FCSTD DOCUMENT  (FreeCAD 0.20R29603 (Git))
Label: letterplate_13_13_V2_freecad
License: All rights reserved
LicenseURL: http://en.wikipedia.org/wiki/All_rights_reserved
objects: Part::Part2DObjectPython×171, App::Part×1
note: 171 computed .brp shape members not serialized (recipe doc carries the construction recipe); baked Part::Feature solids carry a one-line shape summary decoded from their .brp

FEATURE [Part::Part2DObjectPython] Circle  # Draft 2D object (typed FeaturePython)
  Area = 0
  FirstAngle = 0
  LastAngle = 0
  MakeFace = true
  Placement = pos=(275,502.778,0) rot=(0,0,1;0rad)
  Radius = 2.56
FEATURE [Part::Part2DObjectPython] ShapeString  # Draft 2D object (typed FeaturePython)
  FontFile = <path> macros/fonts/LiberationMono-V2.ttf
  MakeFace = true
  Placement = pos=(64.8,463.626,0) rot=(0,0,1;0rad)
  Size = 25.5
  Tracking = 0
FEATURE [Part::Part2DObjectPython] ShapeString001  # Draft 2D object (typed FeaturePython)
  FontFile = <path> macros/fonts/LiberationMono-V2.ttf
  MakeFace = true
  Placement = pos=(98.1333,463.626,0) rot=(0,0,1;0rad)
  Size = 25.5
  Tracking = 0
FEATURE [Part::Part2DObjectPython] ShapeString002  # Draft 2D object (typed FeaturePython)
  FontFile = <path> macros/fonts/LiberationMono-V2.ttf
  MakeFace = true
  Placement = pos=(131.467,463.626,0) rot=(0,0,1;0rad)
  Size = 25.5
  Tracking = 0
FEATURE [Part::Part2DObjectPython] ShapeString003  # Draft 2D object (typed FeaturePython)
  FontFile = <path> macros/fonts/LiberationMono-V2.ttf
  MakeFace = true
  Placement = pos=(164.8,463.626,0) rot=(0,0,1;0rad)
  Size = 25.5
  Tracking = 0
FEATURE [Part::Part2DObjectPython] ShapeString004  # Draft 2D object (typed FeaturePython)
  FontFile = <path> macros/fonts/LiberationMono-V2.ttf
  MakeFace = true
  Placement = pos=(198.133,463.626,0) rot=(0,0,1;0rad)
  Size = 25.5
  Tracking = 0
FEATURE [Part::Part2DObjectPython] ShapeString005  # Draft 2D object (typed FeaturePython)
  FontFile = <path> macros/fonts/LiberationMono-V2.ttf
  MakeFace = true
  Placement = pos=(231.467,463.626,0) rot=(0,0,1;0rad)
  Size = 25.5
  Tracking = 0
FEATURE [Part::Part2DObjectPython] ShapeString006  # Draft 2D object (typed FeaturePython)
  FontFile = <path> macros/fonts/LiberationMono-V2.ttf
  MakeFace = true
  Placement = pos=(264.8,463.626,0) rot=(0,0,1;0rad)
  Size = 25.5
  Tracking = 0
FEATURE [Part::Part2DObjectPython] ShapeString007  # Draft 2D object (typed FeaturePython)
  FontFile = <path> macros/fonts/LiberationMono-V2.ttf
  MakeFace = true
  Placement = pos=(298.133,463.626,0) rot=(0,0,1;0rad)
  Size = 25.5
  Tracking = 0
FEATURE [Part::Part2DObjectPython] ShapeString008  # Draft 2D object (typed FeaturePython)
  FontFile = <path> macros/fonts/LiberationMono-V2.ttf
  MakeFace = true
  Placement = pos=(331.467,463.626,0) rot=(0,0,1;0rad)
  Size = 25.5
  Tracking = 0
FEATURE [Part::Part2DObjectPython] ShapeString009  # Draft 2D object (typed FeaturePython)
  FontFile = <path> macros/fonts/LiberationMono-V2.ttf
  MakeFace = true
  Placement = pos=(364.8,463.626,0) rot=(0,0,1;0rad)
  Size = 25.5
  Tracking = 0
FEATURE [Part::Part2DObjectPython] ShapeString010  # Draft 2D object (typed FeaturePython)
  FontFile = <path> macros/fonts/LiberationMono-V2.ttf
  MakeFace = true
  Placement = pos=(398.133,463.626,0) rot=(0,0,1;0rad)
  Size = 25.5
  Tracking = 0
FEATURE [Part::Part2DObjectPython] ShapeString011  # Draft 2D object (typed FeaturePython)
  FontFile = <path> macros/fonts/LiberationMono-V2.ttf
  MakeFace = true
  Placement = pos=(431.467,463.626,0) rot=(0,0,1;0rad)
  Size = 25.5
  Tracking = 0
FEATURE [Part::Part2DObjectPython] ShapeString012  # Draft 2D object (typed FeaturePython)
  FontFile = <path> macros/fonts/LiberationMono-V2.ttf
  MakeFace = true
  Placement = pos=(464.8,463.626,0) rot=(0,0,1;0rad)
  Size = 25.5
  Tracking = 0
FEATURE [Part::Part2DObjectPython] ShapeString013  # Draft 2D object (typed FeaturePython)
  FontFile = <path> macros/fonts/LiberationMono-V2.ttf
  MakeFace = true
  Placement = pos=(64.8,430.293,0) rot=(0,0,1;0rad)
  Size = 25.5
  Tracking = 0
FEATURE [Part::Part2DObjectPython] ShapeString014  # Draft 2D object (typed FeaturePython)
  FontFile = <path> macros/fonts/LiberationMono-V2.ttf
  MakeFace = true
  Placement = pos=(98.1333,430.293,0) rot=(0,0,1;0rad)
  Size = 25.5
  String = S
  Tracking = 0
FEATURE [Part::Part2DObjectPython] ShapeString015  # Draft 2D object (typed FeaturePython)
  FontFile = <path> macros/fonts/LiberationMono-V2.ttf
  MakeFace = true
  Placement = pos=(131.467,430.293,0) rot=(0,0,1;0rad)
  Size = 25.5
  String = O
  Tracking = 0
FEATURE [Part::Part2DObjectPython] ShapeString016  # Draft 2D object (typed FeaturePython)
  FontFile = <path> macros/fonts/LiberationMono-V2.ttf
  MakeFace = true
  Placement = pos=(164.8,430.293,0) rot=(0,0,1;0rad)
  Size = 25.5
  String = N
  Tracking = 0
FEATURE [Part::Part2DObjectPython] ShapeString017  # Draft 2D object (typed FeaturePython)
  FontFile = <path> macros/fonts/LiberationMono-V2.ttf
  MakeFace = true
  Placement = pos=(198.133,430.293,0) rot=(0,0,1;0rad)
  Size = 25.5
  String = O
  Tracking = 0
FEATURE [Part::Part2DObjectPython] ShapeString018  # Draft 2D object (typed FeaturePython)
  FontFile = <path> macros/fonts/LiberationMono-V2.ttf
  MakeFace = true
  Placement = pos=(231.467,430.293,0) rot=(0,0,1;0rad)
  Size = 25.5
  String = È
  Tracking = 0
FEATURE [Part::Part2DObjectPython] ShapeString019  # Draft 2D object (typed FeaturePython)
  FontFile = <path> macros/fonts/LiberationMono-V2.ttf
  MakeFace = true
  Placement = pos=(264.8,430.293,0) rot=(0,0,1;0rad)
  Size = 25.5
  String = L
  Tracking = 0
FEATURE [Part::Part2DObjectPython] ShapeString020  # Draft 2D object (typed FeaturePython)
  FontFile = <path> macros/fonts/LiberationMono-V2.ttf
  MakeFace = true
  Placement = pos=(298.133,430.293,0) rot=(0,0,1;0rad)
  Size = 25.5
  String = E
  Tracking = 0
FEATURE [Part::Part2DObjectPython] ShapeString021  # Draft 2D object (typed FeaturePython)
  FontFile = <path> macros/fonts/LiberationMono-V2.ttf
  MakeFace = true
  Placement = pos=(331.467,430.293,0) rot=(0,0,1;0rad)
  Size = 25.5
  String = R
  Tracking = 0
FEATURE [Part::Part2DObjectPython] ShapeString022  # Draft 2D object (typed FeaturePython)
  FontFile = <path> macros/fonts/LiberationMono-V2.ttf
  MakeFace = true
  Placement = pos=(364.8,430.293,0) rot=(0,0,1;0rad)
  Size = 25.5
  String = D
  Tracking = 0
FEATURE [Part::Part2DObjectPython] ShapeString023  # Draft 2D object (typed FeaturePython)
  FontFile = <path> macros/fonts/LiberationMono-V2.ttf
  MakeFace = true
  Placement = pos=(398.133,430.293,0) rot=(0,0,1;0rad)
  Size = 25.5
  String = U
  Tracking = 0
FEATURE [Part::Part2DObjectPython] ShapeString024  # Draft 2D object (typed FeaturePython)
  FontFile = <path> macros/fonts/LiberationMono-V2.ttf
  MakeFace = true
  Placement = pos=(431.467,430.293,0) rot=(0,0,1;0rad)
  Size = 25.5
  String = E
  Tracking = 0
FEATURE [Part::Part2DObjectPython] ShapeString025  # Draft 2D object (typed FeaturePython)
  FontFile = <path> macros/fonts/LiberationMono-V2.ttf
  MakeFace = true
  Placement = pos=(464.8,430.293,0) rot=(0,0,1;0rad)
  Size = 25.5
  Tracking = 0
FEATURE [Part::Part2DObjectPython] ShapeString026  # Draft 2D object (typed FeaturePython)
  FontFile = <path> macros/fonts/LiberationMono-V2.ttf
  MakeFace = true
  Placement = pos=(64.8,396.959,0) rot=(0,0,1;0rad)
  Size = 25.5
  Tracking = 0
FEATURE [Part::Part2DObjectPython] ShapeString027  # Draft 2D object (typed FeaturePython)
  FontFile = <path> macros/fonts/LiberationMono-V2.ttf
  MakeFace = true
  Placement = pos=(98.1333,396.959,0) rot=(0,0,1;0rad)
  Size = 25.5
  String = L
  Tracking = 0
FEATURE [Part::Part2DObjectPython] ShapeString028  # Draft 2D object (typed FeaturePython)
  FontFile = <path> macros/fonts/LiberationMono-V2.ttf
  MakeFace = true
  Placement = pos=(131.467,396.959,0) rot=(0,0,1;0rad)
  Size = 25.5
  String = U
  Tracking = 0
FEATURE [Part::Part2DObjectPython] ShapeString029  # Draft 2D object (typed FeaturePython)
  FontFile = <path> macros/fonts/LiberationMono-V2.ttf
  MakeFace = true
  Placement = pos=(164.8,396.959,0) rot=(0,0,1;0rad)
  Size = 25.5
  String = N
  Tracking = 0
FEATURE [Part::Part2DObjectPython] ShapeString030  # Draft 2D object (typed FeaturePython)
  FontFile = <path> macros/fonts/LiberationMono-V2.ttf
  MakeFace = true
  Placement = pos=(198.133,396.959,0) rot=(0,0,1;0rad)
  Size = 25.5
  String = A
  Tracking = 0
FEATURE [Part::Part2DObjectPython] ShapeString031  # Draft 2D object (typed FeaturePython)
  FontFile = <path> macros/fonts/LiberationMono-V2.ttf
  MakeFace = true
  Placement = pos=(231.467,396.959,0) rot=(0,0,1;0rad)
  Size = 25.5
  String = Q
  Tracking = 0
FEATURE [Part::Part2DObjectPython] ShapeString032  # Draft 2D object (typed FeaturePython)
  FontFile = <path> macros/fonts/LiberationMono-V2.ttf
  MakeFace = true
  Placement = pos=(264.8,396.959,0) rot=(0,0,1;0rad)
  Size = 25.5
  String = U
  Tracking = 0
FEATURE [Part::Part2DObjectPython] ShapeString033  # Draft 2D object (typed FeaturePython)
  FontFile = <path> macros/fonts/LiberationMono-V2.ttf
  MakeFace = true
  Placement = pos=(298.133,396.959,0) rot=(0,0,1;0rad)
  Size = 25.5
  String = A
  Tracking = 0
FEATURE [Part::Part2DObjectPython] ShapeString034  # Draft 2D object (typed FeaturePython)
  FontFile = <path> macros/fonts/LiberationMono-V2.ttf
  MakeFace = true
  Placement = pos=(331.467,396.959,0) rot=(0,0,1;0rad)
  Size = 25.5
  String = T
  Tracking = 0
FEATURE [Part::Part2DObjectPython] ShapeString035  # Draft 2D object (typed FeaturePython)
  FontFile = <path> macros/fonts/LiberationMono-V2.ttf
  MakeFace = true
  Placement = pos=(364.8,396.959,0) rot=(0,0,1;0rad)
  Size = 25.5
  String = T
  Tracking = 0
FEATURE [Part::Part2DObjectPython] ShapeString036  # Draft 2D object (typed FeaturePython)
  FontFile = <path> macros/fonts/LiberationMono-V2.ttf
  MakeFace = true
  Placement = pos=(398.133,396.959,0) rot=(0,0,1;0rad)
  Size = 25.5
  String = R
  Tracking = 0
FEATURE [Part::Part2DObjectPython] ShapeString037  # Draft 2D object (typed FeaturePython)
  FontFile = <path> macros/fonts/LiberationMono-V2.ttf
  MakeFace = true
  Placement = pos=(431.467,396.959,0) rot=(0,0,1;0rad)
  Size = 25.5
  String = O
  Tracking = 0
FEATURE [Part::Part2DObjectPython] ShapeString038  # Draft 2D object (typed FeaturePython)
  FontFile = <path> macros/fonts/LiberationMono-V2.ttf
  MakeFace = true
  Placement = pos=(464.8,396.959,0) rot=(0,0,1;0rad)
  Size = 25.5
  Tracking = 0
FEATURE [Part::Part2DObjectPython] ShapeString039  # Draft 2D object (typed FeaturePython)
  FontFile = <path> macros/fonts/LiberationMono-V2.ttf
  MakeFace = true
  Placement = pos=(64.8,363.626,0) rot=(0,0,1;0rad)
  Size = 25.5
  Tracking = 0
FEATURE [Part::Part2DObjectPython] ShapeString040  # Draft 2D object (typed FeaturePython)
  FontFile = <path> macros/fonts/LiberationMono-V2.ttf
  MakeFace = true
  Placement = pos=(98.1333,363.626,0) rot=(0,0,1;0rad)
  Size = 25.5
  String = S
  Tracking = 0
FEATURE [Part::Part2DObjectPython] ShapeString041  # Draft 2D object (typed FeaturePython)
  FontFile = <path> macros/fonts/LiberationMono-V2.ttf
  MakeFace = true
  Placement = pos=(131.467,363.626,0) rot=(0,0,1;0rad)
  Size = 25.5
  String = E
  Tracking = 0
FEATURE [Part::Part2DObjectPython] ShapeString042  # Draft 2D object (typed FeaturePython)
  FontFile = <path> macros/fonts/LiberationMono-V2.ttf
  MakeFace = true
  Placement = pos=(164.8,363.626,0) rot=(0,0,1;0rad)
  Size = 25.5
  String = T
  Tracking = 0
FEATURE [Part::Part2DObjectPython] ShapeString043  # Draft 2D object (typed FeaturePython)
  FontFile = <path> macros/fonts/LiberationMono-V2.ttf
  MakeFace = true
  Placement = pos=(198.133,363.626,0) rot=(0,0,1;0rad)
  Size = 25.5
  String = T
  Tracking = 0
FEATURE [Part::Part2DObjectPython] ShapeString044  # Draft 2D object (typed FeaturePython)
  FontFile = <path> macros/fonts/LiberationMono-V2.ttf
  MakeFace = true
  Placement = pos=(231.467,363.626,0) rot=(0,0,1;0rad)
  Size = 25.5
  String = E
  Tracking = 0
FEATURE [Part::Part2DObjectPython] ShapeString045  # Draft 2D object (typed FeaturePython)
  FontFile = <path> macros/fonts/LiberationMono-V2.ttf
  MakeFace = true
  Placement = pos=(264.8,363.626,0) rot=(0,0,1;0rad)
  Size = 25.5
  String = D
  Tracking = 0
FEATURE [Part::Part2DObjectPython] ShapeString046  # Draft 2D object (typed FeaturePython)
  FontFile = <path> macros/fonts/LiberationMono-V2.ttf
  MakeFace = true
  Placement = pos=(298.133,363.626,0) rot=(0,0,1;0rad)
  Size = 25.5
  String = O
  Tracking = 0
FEATURE [Part::Part2DObjectPython] ShapeString047  # Draft 2D object (typed FeaturePython)
  FontFile = <path> macros/fonts/LiberationMono-V2.ttf
  MakeFace = true
  Placement = pos=(331.467,363.626,0) rot=(0,0,1;0rad)
  Size = 25.5
  String = D
  Tracking = 0
FEATURE [Part::Part2DObjectPython] ShapeString048  # Draft 2D object (typed FeaturePython)
  FontFile = <path> macros/fonts/LiberationMono-V2.ttf
  MakeFace = true
  Placement = pos=(364.8,363.626,0) rot=(0,0,1;0rad)
  Size = 25.5
  String = I
  Tracking = 0
FEATURE [Part::Part2DObjectPython] ShapeString049  # Draft 2D object (typed FeaturePython)
  FontFile = <path> macros/fonts/LiberationMono-V2.ttf
  MakeFace = true
  Placement = pos=(398.133,363.626,0) rot=(0,0,1;0rad)
  Size = 25.5
  String = C
  Tracking = 0
FEATURE [Part::Part2DObjectPython] ShapeString050  # Draft 2D object (typed FeaturePython)
  FontFile = <path> macros/fonts/LiberationMono-V2.ttf
  MakeFace = true
  Placement = pos=(431.467,363.626,0) rot=(0,0,1;0rad)
  Size = 25.5
  String = I
  Tracking = 0
FEATURE [Part::Part2DObjectPython] ShapeString051  # Draft 2D object (typed FeaturePython)
  FontFile = <path> macros/fonts/LiberationMono-V2.ttf
  MakeFace = true
  Placement = pos=(464.8,363.626,0) rot=(0,0,1;0rad)
  Size = 25.5
  Tracking = 0
FEATURE [Part::Part2DObjectPython] ShapeString052  # Draft 2D object (typed FeaturePython)
  FontFile = <path> macros/fonts/LiberationMono-V2.ttf
  MakeFace = true
  Placement = pos=(64.8,330.293,0) rot=(0,0,1;0rad)
  Size = 25.5
  Tracking = 0
FEATURE [Part::Part2DObjectPython] ShapeString053  # Draft 2D object (typed FeaturePython)
  FontFile = <path> macros/fonts/LiberationMono-V2.ttf
  MakeFace = true
  Placement = pos=(98.1333,330.293,0) rot=(0,0,1;0rad)
  Size = 25.5
  String = S
  Tracking = 0
FEATURE [Part::Part2DObjectPython] ShapeString054  # Draft 2D object (typed FeaturePython)
  FontFile = <path> macros/fonts/LiberationMono-V2.ttf
  MakeFace = true
  Placement = pos=(131.467,330.293,0) rot=(0,0,1;0rad)
  Size = 25.5
  String = E
  Tracking = 0
FEATURE [Part::Part2DObjectPython] ShapeString055  # Draft 2D object (typed FeaturePython)
  FontFile = <path> macros/fonts/LiberationMono-V2.ttf
  MakeFace = true
  Placement = pos=(164.8,330.293,0) rot=(0,0,1;0rad)
  Size = 25.5
  String = I
  Tracking = 0
FEATURE [Part::Part2DObjectPython] ShapeString056  # Draft 2D object (typed FeaturePython)
  FontFile = <path> macros/fonts/LiberationMono-V2.ttf
  MakeFace = true
  Placement = pos=(198.133,330.293,0) rot=(0,0,1;0rad)
  Size = 25.5
  String = N
  Tracking = 0
FEATURE [Part::Part2DObjectPython] ShapeString057  # Draft 2D object (typed FeaturePython)
  FontFile = <path> macros/fonts/LiberationMono-V2.ttf
  MakeFace = true
  Placement = pos=(231.467,330.293,0) rot=(0,0,1;0rad)
  Size = 25.5
  String = O
  Tracking = 0
FEATURE [Part::Part2DObjectPython] ShapeString058  # Draft 2D object (typed FeaturePython)
  FontFile = <path> macros/fonts/LiberationMono-V2.ttf
  MakeFace = true
  Placement = pos=(264.8,330.293,0) rot=(0,0,1;0rad)
  Size = 25.5
  String = V
  Tracking = 0
FEATURE [Part::Part2DObjectPython] ShapeString059  # Draft 2D object (typed FeaturePython)
  FontFile = <path> macros/fonts/LiberationMono-V2.ttf
  MakeFace = true
  Placement = pos=(298.133,330.293,0) rot=(0,0,1;0rad)
  Size = 25.5
  String = E
  Tracking = 0
FEATURE [Part::Part2DObjectPython] ShapeString060  # Draft 2D object (typed FeaturePython)
  FontFile = <path> macros/fonts/LiberationMono-V2.ttf
  MakeFace = true
  Placement = pos=(331.467,330.293,0) rot=(0,0,1;0rad)
  Size = 25.5
  String = O
  Tracking = 0
FEATURE [Part::Part2DObjectPython] ShapeString061  # Draft 2D object (typed FeaturePython)
  FontFile = <path> macros/fonts/LiberationMono-V2.ttf
  MakeFace = true
  Placement = pos=(364.8,330.293,0) rot=(0,0,1;0rad)
  Size = 25.5
  String = T
  Tracking = 0
FEATURE [Part::Part2DObjectPython] ShapeString062  # Draft 2D object (typed FeaturePython)
  FontFile = <path> macros/fonts/LiberationMono-V2.ttf
  MakeFace = true
  Placement = pos=(398.133,330.293,0) rot=(0,0,1;0rad)
  Size = 25.5
  String = T
  Tracking = 0
FEATURE [Part::Part2DObjectPython] ShapeString063  # Draft 2D object (typed FeaturePython)
  FontFile = <path> macros/fonts/LiberationMono-V2.ttf
  MakeFace = true
  Placement = pos=(431.467,330.293,0) rot=(0,0,1;0rad)
  Size = 25.5
  String = O
  Tracking = 0
FEATURE [Part::Part2DObjectPython] ShapeString064  # Draft 2D object (typed FeaturePython)
  FontFile = <path> macros/fonts/LiberationMono-V2.ttf
  MakeFace = true
  Placement = pos=(464.8,330.293,0) rot=(0,0,1;0rad)
  Size = 25.5
  Tracking = 0
FEATURE [Part::Part2DObjectPython] ShapeString065  # Draft 2D object (typed FeaturePython)
  FontFile = <path> macros/fonts/LiberationMono-V2.ttf
  MakeFace = true
  Placement = pos=(64.8,296.959,0) rot=(0,0,1;0rad)
  Size = 25.5
  Tracking = 0
FEATURE [Part::Part2DObjectPython] ShapeString066  # Draft 2D object (typed FeaturePython)
  FontFile = <path> macros/fonts/LiberationMono-V2.ttf
  MakeFace = true
  Placement = pos=(98.1333,296.959,0) rot=(0,0,1;0rad)
  Size = 25.5
  String = C
  Tracking = 0
FEATURE [Part::Part2DObjectPython] ShapeString067  # Draft 2D object (typed FeaturePython)
  FontFile = <path> macros/fonts/LiberationMono-V2.ttf
  MakeFace = true
  Placement = pos=(131.467,296.959,0) rot=(0,0,1;0rad)
  Size = 25.5
  String = I
  Tracking = 0
FEATURE [Part::Part2DObjectPython] ShapeString068  # Draft 2D object (typed FeaturePython)
  FontFile = <path> macros/fonts/LiberationMono-V2.ttf
  MakeFace = true
  Placement = pos=(164.8,296.959,0) rot=(0,0,1;0rad)
  Size = 25.5
  String = N
  Tracking = 0
FEATURE [Part::Part2DObjectPython] ShapeString069  # Draft 2D object (typed FeaturePython)
  FontFile = <path> macros/fonts/LiberationMono-V2.ttf
  MakeFace = true
  Placement = pos=(198.133,296.959,0) rot=(0,0,1;0rad)
  Size = 25.5
  String = Q
  Tracking = 0
FEATURE [Part::Part2DObjectPython] ShapeString070  # Draft 2D object (typed FeaturePython)
  FontFile = <path> macros/fonts/LiberationMono-V2.ttf
  MakeFace = true
  Placement = pos=(231.467,296.959,0) rot=(0,0,1;0rad)
  Size = 25.5
  String = U
  Tracking = 0
FEATURE [Part::Part2DObjectPython] ShapeString071  # Draft 2D object (typed FeaturePython)
  FontFile = <path> macros/fonts/LiberationMono-V2.ttf
  MakeFace = true
  Placement = pos=(264.8,296.959,0) rot=(0,0,1;0rad)
  Size = 25.5
  String = E
  Tracking = 0
FEATURE [Part::Part2DObjectPython] ShapeString072  # Draft 2D object (typed FeaturePython)
  FontFile = <path> macros/fonts/LiberationMono-V2.ttf
  MakeFace = true
  Placement = pos=(298.133,296.959,0) rot=(0,0,1;0rad)
  Size = 25.5
  String = D
  Tracking = 0
FEATURE [Part::Part2DObjectPython] ShapeString073  # Draft 2D object (typed FeaturePython)
  FontFile = <path> macros/fonts/LiberationMono-V2.ttf
  MakeFace = true
  Placement = pos=(331.467,296.959,0) rot=(0,0,1;0rad)
  Size = 25.5
  String = I
  Tracking = 0
FEATURE [Part::Part2DObjectPython] ShapeString074  # Draft 2D object (typed FeaturePython)
  FontFile = <path> macros/fonts/LiberationMono-V2.ttf
  MakeFace = true
  Placement = pos=(364.8,296.959,0) rot=(0,0,1;0rad)
  Size = 25.5
  String = E
  Tracking = 0
FEATURE [Part::Part2DObjectPython] ShapeString075  # Draft 2D object (typed FeaturePython)
  FontFile = <path> macros/fonts/LiberationMono-V2.ttf
  MakeFace = true
  Placement = pos=(398.133,296.959,0) rot=(0,0,1;0rad)
  Size = 25.5
  String = C
  Tracking = 0
FEATURE [Part::Part2DObjectPython] ShapeString076  # Draft 2D object (typed FeaturePython)
  FontFile = <path> macros/fonts/LiberationMono-V2.ttf
  MakeFace = true
  Placement = pos=(431.467,296.959,0) rot=(0,0,1;0rad)
  Size = 25.5
  String = I
  Tracking = 0
FEATURE [Part::Part2DObjectPython] ShapeString077  # Draft 2D object (typed FeaturePython)
  FontFile = <path> macros/fonts/LiberationMono-V2.ttf
  MakeFace = true
  Placement = pos=(464.8,296.959,0) rot=(0,0,1;0rad)
  Size = 25.5
  Tracking = 0
FEATURE [Part::Part2DObjectPython] ShapeString078  # Draft 2D object (typed FeaturePython)
  FontFile = <path> macros/fonts/LiberationMono-V2.ttf
  MakeFace = true
  Placement = pos=(64.8,263.626,0) rot=(0,0,1;0rad)
  Size = 25.5
  Tracking = 0
FEATURE [Part::Part2DObjectPython] ShapeString079  # Draft 2D object (typed FeaturePython)
  FontFile = <path> macros/fonts/LiberationMono-V2.ttf
  MakeFace = true
  Placement = pos=(98.1333,263.626,0) rot=(0,0,1;0rad)
  Size = 25.5
  String = U
  Tracking = 0
FEATURE [Part::Part2DObjectPython] ShapeString080  # Draft 2D object (typed FeaturePython)
  FontFile = <path> macros/fonts/LiberationMono-V2.ttf
  MakeFace = true
  Placement = pos=(131.467,263.626,0) rot=(0,0,1;0rad)
  Size = 25.5
  String = N
  Tracking = 0
FEATURE [Part::Part2DObjectPython] ShapeString081  # Draft 2D object (typed FeaturePython)
  FontFile = <path> macros/fonts/LiberationMono-V2.ttf
  MakeFace = true
  Placement = pos=(164.8,263.626,0) rot=(0,0,1;0rad)
  Size = 25.5
  String = D
  Tracking = 0
FEATURE [Part::Part2DObjectPython] ShapeString082  # Draft 2D object (typed FeaturePython)
  FontFile = <path> macros/fonts/LiberationMono-V2.ttf
  MakeFace = true
  Placement = pos=(198.133,263.626,0) rot=(0,0,1;0rad)
  Size = 25.5
  String = I
  Tracking = 0
FEATURE [Part::Part2DObjectPython] ShapeString083  # Draft 2D object (typed FeaturePython)
  FontFile = <path> macros/fonts/LiberationMono-V2.ttf
  MakeFace = true
  Placement = pos=(231.467,263.626,0) rot=(0,0,1;0rad)
  Size = 25.5
  String = C
  Tracking = 0
FEATURE [Part::Part2DObjectPython] ShapeString084  # Draft 2D object (typed FeaturePython)
  FontFile = <path> macros/fonts/LiberationMono-V2.ttf
  MakeFace = true
  Placement = pos=(264.8,263.626,0) rot=(0,0,1;0rad)
  Size = 25.5
  String = I
  Tracking = 0
FEATURE [Part::Part2DObjectPython] ShapeString085  # Draft 2D object (typed FeaturePython)
  FontFile = <path> macros/fonts/LiberationMono-V2.ttf
  MakeFace = true
  Placement = pos=(298.133,263.626,0) rot=(0,0,1;0rad)
  Size = 25.5
  String = T
  Tracking = 0
FEATURE [Part::Part2DObjectPython] ShapeString086  # Draft 2D object (typed FeaturePython)
  FontFile = <path> macros/fonts/LiberationMono-V2.ttf
  MakeFace = true
  Placement = pos=(331.467,263.626,0) rot=(0,0,1;0rad)
  Size = 25.5
  String = R
  Tracking = 0
FEATURE [Part::Part2DObjectPython] ShapeString087  # Draft 2D object (typed FeaturePython)
  FontFile = <path> macros/fonts/LiberationMono-V2.ttf
  MakeFace = true
  Placement = pos=(364.8,263.626,0) rot=(0,0,1;0rad)
  Size = 25.5
  String = E
  Tracking = 0
FEATURE [Part::Part2DObjectPython] ShapeString088  # Draft 2D object (typed FeaturePython)
  FontFile = <path> macros/fonts/LiberationMono-V2.ttf
  MakeFace = true
  Placement = pos=(398.133,263.626,0) rot=(0,0,1;0rad)
  Size = 25.5
  String = V
  Tracking = 0
FEATURE [Part::Part2DObjectPython] ShapeString089  # Draft 2D object (typed FeaturePython)
  FontFile = <path> macros/fonts/LiberationMono-V2.ttf
  MakeFace = true
  Placement = pos=(431.467,263.626,0) rot=(0,0,1;0rad)
  Size = 25.5
  String = E
  Tracking = 0
FEATURE [Part::Part2DObjectPython] ShapeString090  # Draft 2D object (typed FeaturePython)
  FontFile = <path> macros/fonts/LiberationMono-V2.ttf
  MakeFace = true
  Placement = pos=(464.8,263.626,0) rot=(0,0,1;0rad)
  Size = 25.5
  Tracking = 0
FEATURE [Part::Part2DObjectPython] ShapeString091  # Draft 2D object (typed FeaturePython)
  FontFile = <path> macros/fonts/LiberationMono-V2.ttf
  MakeFace = true
  Placement = pos=(64.8,230.293,0) rot=(0,0,1;0rad)
  Size = 25.5
  Tracking = 0
FEATURE [Part::Part2DObjectPython] ShapeString092  # Draft 2D object (typed FeaturePython)
  FontFile = <path> macros/fonts/LiberationMono-V2.ttf
  MakeFace = true
  Placement = pos=(98.1333,230.293,0) rot=(0,0,1;0rad)
  Size = 25.5
  String = M
  Tracking = 0
FEATURE [Part::Part2DObjectPython] ShapeString093  # Draft 2D object (typed FeaturePython)
  FontFile = <path> macros/fonts/LiberationMono-V2.ttf
  MakeFace = true
  Placement = pos=(131.467,230.293,0) rot=(0,0,1;0rad)
  Size = 25.5
  String = E
  Tracking = 0
FEATURE [Part::Part2DObjectPython] ShapeString094  # Draft 2D object (typed FeaturePython)
  FontFile = <path> macros/fonts/LiberationMono-V2.ttf
  MakeFace = true
  Placement = pos=(164.8,230.293,0) rot=(0,0,1;0rad)
  Size = 25.5
  String = N
  Tracking = 0
FEATURE [Part::Part2DObjectPython] ShapeString095  # Draft 2D object (typed FeaturePython)
  FontFile = <path> macros/fonts/LiberationMono-V2.ttf
  MakeFace = true
  Placement = pos=(198.133,230.293,0) rot=(0,0,1;0rad)
  Size = 25.5
  String = O
  Tracking = 0
FEATURE [Part::Part2DObjectPython] ShapeString096  # Draft 2D object (typed FeaturePython)
  FontFile = <path> macros/fonts/LiberationMono-V2.ttf
  MakeFace = true
  Placement = pos=(231.467,230.293,0) rot=(0,0,1;0rad)
  Size = 25.5
  String = B
  Tracking = 0
FEATURE [Part::Part2DObjectPython] ShapeString097  # Draft 2D object (typed FeaturePython)
  FontFile = <path> macros/fonts/LiberationMono-V2.ttf
  MakeFace = true
  Placement = pos=(264.8,230.293,0) rot=(0,0,1;0rad)
  Size = 25.5
  String = T
  Tracking = 0
FEATURE [Part::Part2DObjectPython] ShapeString098  # Draft 2D object (typed FeaturePython)
  FontFile = <path> macros/fonts/LiberationMono-V2.ttf
  MakeFace = true
  Placement = pos=(298.133,230.293,0) rot=(0,0,1;0rad)
  Size = 25.5
  String = R
  Tracking = 0
FEATURE [Part::Part2DObjectPython] ShapeString099  # Draft 2D object (typed FeaturePython)
  FontFile = <path> macros/fonts/LiberationMono-V2.ttf
  MakeFace = true
  Placement = pos=(331.467,230.293,0) rot=(0,0,1;0rad)
  Size = 25.5
  String = E
  Tracking = 0
FEATURE [Part::Part2DObjectPython] ShapeString100  # Draft 2D object (typed FeaturePython)
  FontFile = <path> macros/fonts/LiberationMono-V2.ttf
  MakeFace = true
  Placement = pos=(364.8,230.293,0) rot=(0,0,1;0rad)
  Size = 25.5
  String = N
  Tracking = 0
FEATURE [Part::Part2DObjectPython] ShapeString101  # Draft 2D object (typed FeaturePython)
  FontFile = <path> macros/fonts/LiberationMono-V2.ttf
  MakeFace = true
  Placement = pos=(398.133,230.293,0) rot=(0,0,1;0rad)
  Size = 25.5
  String = T
  Tracking = 0
FEATURE [Part::Part2DObjectPython] ShapeString102  # Draft 2D object (typed FeaturePython)
  FontFile = <path> macros/fonts/LiberationMono-V2.ttf
  MakeFace = true
  Placement = pos=(431.467,230.293,0) rot=(0,0,1;0rad)
  Size = 25.5
  String = A
  Tracking = 0
FEATURE [Part::Part2DObjectPython] ShapeString103  # Draft 2D object (typed FeaturePython)
  FontFile = <path> macros/fonts/LiberationMono-V2.ttf
  MakeFace = true
  Placement = pos=(464.8,230.293,0) rot=(0,0,1;0rad)
  Size = 25.5
  Tracking = 0
FEATURE [Part::Part2DObjectPython] ShapeString104  # Draft 2D object (typed FeaturePython)
  FontFile = <path> macros/fonts/LiberationMono-V2.ttf
  MakeFace = true
  Placement = pos=(64.8,196.959,0) rot=(0,0,1;0rad)
  Size = 25.5
  Tracking = 0
FEATURE [Part::Part2DObjectPython] ShapeString105  # Draft 2D object (typed FeaturePython)
  FontFile = <path> macros/fonts/LiberationMono-V2.ttf
  MakeFace = true
  Placement = pos=(98.1333,196.959,0) rot=(0,0,1;0rad)
  Size = 25.5
  String = E
  Tracking = 0
FEATURE [Part::Part2DObjectPython] ShapeString106  # Draft 2D object (typed FeaturePython)
  FontFile = <path> macros/fonts/LiberationMono-V2.ttf
  MakeFace = true
  Placement = pos=(131.467,196.959,0) rot=(0,0,1;0rad)
  Size = 25.5
  String = Q
  Tracking = 0
FEATURE [Part::Part2DObjectPython] ShapeString107  # Draft 2D object (typed FeaturePython)
  FontFile = <path> macros/fonts/LiberationMono-V2.ttf
  MakeFace = true
  Placement = pos=(164.8,196.959,0) rot=(0,0,1;0rad)
  Size = 25.5
  String = T
  Tracking = 0
FEATURE [Part::Part2DObjectPython] ShapeString108  # Draft 2D object (typed FeaturePython)
  FontFile = <path> macros/fonts/LiberationMono-V2.ttf
  MakeFace = true
  Placement = pos=(198.133,196.959,0) rot=(0,0,1;0rad)
  Size = 25.5
  String = U
  Tracking = 0
FEATURE [Part::Part2DObjectPython] ShapeString109  # Draft 2D object (typed FeaturePython)
  FontFile = <path> macros/fonts/LiberationMono-V2.ttf
  MakeFace = true
  Placement = pos=(231.467,196.959,0) rot=(0,0,1;0rad)
  Size = 25.5
  String = N
  Tracking = 0
FEATURE [Part::Part2DObjectPython] ShapeString110  # Draft 2D object (typed FeaturePython)
  FontFile = <path> macros/fonts/LiberationMono-V2.ttf
  MakeFace = true
  Placement = pos=(264.8,196.959,0) rot=(0,0,1;0rad)
  Size = 25.5
  String = A
  Tracking = 0
FEATURE [Part::Part2DObjectPython] ShapeString111  # Draft 2D object (typed FeaturePython)
  FontFile = <path> macros/fonts/LiberationMono-V2.ttf
  MakeFace = true
  Placement = pos=(298.133,196.959,0) rot=(0,0,1;0rad)
  Size = 25.5
  String = D
  Tracking = 0
FEATURE [Part::Part2DObjectPython] ShapeString112  # Draft 2D object (typed FeaturePython)
  FontFile = <path> macros/fonts/LiberationMono-V2.ttf
  MakeFace = true
  Placement = pos=(331.467,196.959,0) rot=(0,0,1;0rad)
  Size = 25.5
  String = I
  Tracking = 0
FEATURE [Part::Part2DObjectPython] ShapeString113  # Draft 2D object (typed FeaturePython)
  FontFile = <path> macros/fonts/LiberationMono-V2.ttf
  MakeFace = true
  Placement = pos=(364.8,196.959,0) rot=(0,0,1;0rad)
  Size = 25.5
  String = E
  Tracking = 0
FEATURE [Part::Part2DObjectPython] ShapeString114  # Draft 2D object (typed FeaturePython)
  FontFile = <path> macros/fonts/LiberationMono-V2.ttf
  MakeFace = true
  Placement = pos=(398.133,196.959,0) rot=(0,0,1;0rad)
  Size = 25.5
  String = C
  Tracking = 0
FEATURE [Part::Part2DObjectPython] ShapeString115  # Draft 2D object (typed FeaturePython)
  FontFile = <path> macros/fonts/LiberationMono-V2.ttf
  MakeFace = true
  Placement = pos=(431.467,196.959,0) rot=(0,0,1;0rad)
  Size = 25.5
  String = I
  Tracking = 0
FEATURE [Part::Part2DObjectPython] ShapeString116  # Draft 2D object (typed FeaturePython)
  FontFile = <path> macros/fonts/LiberationMono-V2.ttf
  MakeFace = true
  Placement = pos=(464.8,196.959,0) rot=(0,0,1;0rad)
  Size = 25.5
  Tracking = 0
FEATURE [Part::Part2DObjectPython] ShapeString117  # Draft 2D object (typed FeaturePython)
  FontFile = <path> macros/fonts/LiberationMono-V2.ttf
  MakeFace = true
  Placement = pos=(64.8,163.626,0) rot=(0,0,1;0rad)
  Size = 25.5
  Tracking = 0
FEATURE [Part::Part2DObjectPython] ShapeString118  # Draft 2D object (typed FeaturePython)
  FontFile = <path> macros/fonts/LiberationMono-V2.ttf
  MakeFace = true
  Placement = pos=(98.1333,163.626,0) rot=(0,0,1;0rad)
  Size = 25.5
  String = M
  Tracking = 0
FEATURE [Part::Part2DObjectPython] ShapeString119  # Draft 2D object (typed FeaturePython)
  FontFile = <path> macros/fonts/LiberationMono-V2.ttf
  MakeFace = true
  Placement = pos=(131.467,163.626,0) rot=(0,0,1;0rad)
  Size = 25.5
  String = E
  Tracking = 0
FEATURE [Part::Part2DObjectPython] ShapeString120  # Draft 2D object (typed FeaturePython)
  FontFile = <path> macros/fonts/LiberationMono-V2.ttf
  MakeFace = true
  Placement = pos=(164.8,163.626,0) rot=(0,0,1;0rad)
  Size = 25.5
  String = Z
  Tracking = 0
FEATURE [Part::Part2DObjectPython] ShapeString121  # Draft 2D object (typed FeaturePython)
  FontFile = <path> macros/fonts/LiberationMono-V2.ttf
  MakeFace = true
  Placement = pos=(198.133,163.626,0) rot=(0,0,1;0rad)
  Size = 25.5
  String = Z
  Tracking = 0
FEATURE [Part::Part2DObjectPython] ShapeString122  # Draft 2D object (typed FeaturePython)
  FontFile = <path> macros/fonts/LiberationMono-V2.ttf
  MakeFace = true
  Placement = pos=(231.467,163.626,0) rot=(0,0,1;0rad)
  Size = 25.5
  String = O
  Tracking = 0
FEATURE [Part::Part2DObjectPython] ShapeString123  # Draft 2D object (typed FeaturePython)
  FontFile = <path> macros/fonts/LiberationMono-V2.ttf
  MakeFace = true
  Placement = pos=(264.8,163.626,0) rot=(0,0,1;0rad)
  Size = 25.5
  String = Q
  Tracking = 0
FEATURE [Part::Part2DObjectPython] ShapeString124  # Draft 2D object (typed FeaturePython)
  FontFile = <path> macros/fonts/LiberationMono-V2.ttf
  MakeFace = true
  Placement = pos=(298.133,163.626,0) rot=(0,0,1;0rad)
  Size = 25.5
  String = U
  Tracking = 0
FEATURE [Part::Part2DObjectPython] ShapeString125  # Draft 2D object (typed FeaturePython)
  FontFile = <path> macros/fonts/LiberationMono-V2.ttf
  MakeFace = true
  Placement = pos=(331.467,163.626,0) rot=(0,0,1;0rad)
  Size = 25.5
  String = A
  Tracking = 0
FEATURE [Part::Part2DObjectPython] ShapeString126  # Draft 2D object (typed FeaturePython)
  FontFile = <path> macros/fonts/LiberationMono-V2.ttf
  MakeFace = true
  Placement = pos=(364.8,163.626,0) rot=(0,0,1;0rad)
  Size = 25.5
  String = R
  Tracking = 0
FEATURE [Part::Part2DObjectPython] ShapeString127  # Draft 2D object (typed FeaturePython)
  FontFile = <path> macros/fonts/LiberationMono-V2.ttf
  MakeFace = true
  Placement = pos=(398.133,163.626,0) rot=(0,0,1;0rad)
  Size = 25.5
  String = T
  Tracking = 0
FEATURE [Part::Part2DObjectPython] ShapeString128  # Draft 2D object (typed FeaturePython)
  FontFile = <path> macros/fonts/LiberationMono-V2.ttf
  MakeFace = true
  Placement = pos=(431.467,163.626,0) rot=(0,0,1;0rad)
  Size = 25.5
  String = O
  Tracking = 0
FEATURE [Part::Part2DObjectPython] ShapeString129  # Draft 2D object (typed FeaturePython)
  FontFile = <path> macros/fonts/LiberationMono-V2.ttf
  MakeFace = true
  Placement = pos=(464.8,163.626,0) rot=(0,0,1;0rad)
  Size = 25.5
  Tracking = 0
FEATURE [Part::Part2DObjectPython] ShapeString130  # Draft 2D object (typed FeaturePython)
  FontFile = <path> macros/fonts/LiberationMono-V2.ttf
  MakeFace = true
  Placement = pos=(64.8,130.293,0) rot=(0,0,1;0rad)
  Size = 25.5
  Tracking = 0
FEATURE [Part::Part2DObjectPython] ShapeString131  # Draft 2D object (typed FeaturePython)
  FontFile = <path> macros/fonts/LiberationMono-V2.ttf
  MakeFace = true
  Placement = pos=(98.1333,130.293,0) rot=(0,0,1;0rad)
  Size = 25.5
  String = V
  Tracking = 0
FEATURE [Part::Part2DObjectPython] ShapeString132  # Draft 2D object (typed FeaturePython)
  FontFile = <path> macros/fonts/LiberationMono-V2.ttf
  MakeFace = true
  Placement = pos=(131.467,130.293,0) rot=(0,0,1;0rad)
  Size = 25.5
  String = E
  Tracking = 0
FEATURE [Part::Part2DObjectPython] ShapeString133  # Draft 2D object (typed FeaturePython)
  FontFile = <path> macros/fonts/LiberationMono-V2.ttf
  MakeFace = true
  Placement = pos=(164.8,130.293,0) rot=(0,0,1;0rad)
  Size = 25.5
  String = N
  Tracking = 0
FEATURE [Part::Part2DObjectPython] ShapeString134  # Draft 2D object (typed FeaturePython)
  FontFile = <path> macros/fonts/LiberationMono-V2.ttf
  MakeFace = true
  Placement = pos=(198.133,130.293,0) rot=(0,0,1;0rad)
  Size = 25.5
  String = T
  Tracking = 0
FEATURE [Part::Part2DObjectPython] ShapeString135  # Draft 2D object (typed FeaturePython)
  FontFile = <path> macros/fonts/LiberationMono-V2.ttf
  MakeFace = true
  Placement = pos=(231.467,130.293,0) rot=(0,0,1;0rad)
  Size = 25.5
  String = I
  Tracking = 0
FEATURE [Part::Part2DObjectPython] ShapeString136  # Draft 2D object (typed FeaturePython)
  FontFile = <path> macros/fonts/LiberationMono-V2.ttf
  MakeFace = true
  Placement = pos=(264.8,130.293,0) rot=(0,0,1;0rad)
  Size = 25.5
  String = X
  Tracking = 0
FEATURE [Part::Part2DObjectPython] ShapeString137  # Draft 2D object (typed FeaturePython)
  FontFile = <path> macros/fonts/LiberationMono-V2.ttf
  MakeFace = true
  Placement = pos=(298.133,130.293,0) rot=(0,0,1;0rad)
  Size = 25.5
  String = M
  Tracking = 0
FEATURE [Part::Part2DObjectPython] ShapeString138  # Draft 2D object (typed FeaturePython)
  FontFile = <path> macros/fonts/LiberationMono-V2.ttf
  MakeFace = true
  Placement = pos=(331.467,130.293,0) rot=(0,0,1;0rad)
  Size = 25.5
  String = E
  Tracking = 0
FEATURE [Part::Part2DObjectPython] ShapeString139  # Draft 2D object (typed FeaturePython)
  FontFile = <path> macros/fonts/LiberationMono-V2.ttf
  MakeFace = true
  Placement = pos=(364.8,130.293,0) rot=(0,0,1;0rad)
  Size = 25.5
  String = Z
  Tracking = 0
FEATURE [Part::Part2DObjectPython] ShapeString140  # Draft 2D object (typed FeaturePython)
  FontFile = <path> macros/fonts/LiberationMono-V2.ttf
  MakeFace = true
  Placement = pos=(398.133,130.293,0) rot=(0,0,1;0rad)
  Size = 25.5
  String = Z
  Tracking = 0
FEATURE [Part::Part2DObjectPython] ShapeString141  # Draft 2D object (typed FeaturePython)
  FontFile = <path> macros/fonts/LiberationMono-V2.ttf
  MakeFace = true
  Placement = pos=(431.467,130.293,0) rot=(0,0,1;0rad)
  Size = 25.5
  String = A
  Tracking = 0
FEATURE [Part::Part2DObjectPython] ShapeString142  # Draft 2D object (typed FeaturePython)
  FontFile = <path> macros/fonts/LiberationMono-V2.ttf
  MakeFace = true
  Placement = pos=(464.8,130.293,0) rot=(0,0,1;0rad)
  Size = 25.5
  Tracking = 0
FEATURE [Part::Part2DObjectPython] ShapeString143  # Draft 2D object (typed FeaturePython)
  FontFile = <path> macros/fonts/LiberationMono-V2.ttf
  MakeFace = true
  Placement = pos=(64.8,96.9594,0) rot=(0,0,1;0rad)
  Size = 25.5
  Tracking = 0
FEATURE [Part::Part2DObjectPython] ShapeString144  # Draft 2D object (typed FeaturePython)
  FontFile = <path> macros/fonts/LiberationMono-V2.ttf
  MakeFace = true
  Placement = pos=(98.1333,96.9594,0) rot=(0,0,1;0rad)
  Size = 25.5
  String = C
  Tracking = 0
FEATURE [Part::Part2DObjectPython] ShapeString145  # Draft 2D object (typed FeaturePython)
  FontFile = <path> macros/fonts/LiberationMono-V2.ttf
  MakeFace = true
  Placement = pos=(131.467,96.9594,0) rot=(0,0,1;0rad)
  Size = 25.5
  String = I
  Tracking = 0
FEATURE [Part::Part2DObjectPython] ShapeString146  # Draft 2D object (typed FeaturePython)
  FontFile = <path> macros/fonts/LiberationMono-V2.ttf
  MakeFace = true
  Placement = pos=(164.8,96.9594,0) rot=(0,0,1;0rad)
  Size = 25.5
  String = N
  Tracking = 0
FEATURE [Part::Part2DObjectPython] ShapeString147  # Draft 2D object (typed FeaturePython)
  FontFile = <path> macros/fonts/LiberationMono-V2.ttf
  MakeFace = true
  Placement = pos=(198.133,96.9594,0) rot=(0,0,1;0rad)
  Size = 25.5
  String = Q
  Tracking = 0
FEATURE [Part::Part2DObjectPython] ShapeString148  # Draft 2D object (typed FeaturePython)
  FontFile = <path> macros/fonts/LiberationMono-V2.ttf
  MakeFace = true
  Placement = pos=(231.467,96.9594,0) rot=(0,0,1;0rad)
  Size = 25.5
  String = U
  Tracking = 0
FEATURE [Part::Part2DObjectPython] ShapeString149  # Draft 2D object (typed FeaturePython)
  FontFile = <path> macros/fonts/LiberationMono-V2.ttf
  MakeFace = true
  Placement = pos=(264.8,96.9594,0) rot=(0,0,1;0rad)
  Size = 25.5
  String = E
  Tracking = 0
FEATURE [Part::Part2DObjectPython] ShapeString150  # Draft 2D object (typed FeaturePython)
  FontFile = <path> macros/fonts/LiberationMono-V2.ttf
  MakeFace = true
  Placement = pos=(298.133,96.9594,0) rot=(0,0,1;0rad)
  Size = 25.5
  String = R
  Tracking = 0
FEATURE [Part::Part2DObjectPython] ShapeString151 .. ShapeString154  x4 (patterned run collapsed; names and placements below)
  FontFile = <path> macros/fonts/LiberationMono-V2.ttf
  MakeFace = true
  Size = 25.5
  String = *
  Tracking = 0
  placements: 4 in arithmetic series — first pos=(331.467,96.9594,0) rot=(0,0,1;0rad), step (33.3333,0,0), last pos=(431.467,96.9594,0) rot=(0,0,1;0rad)
FEATURE [Part::Part2DObjectPython] ShapeString155  # Draft 2D object (typed FeaturePython)
  FontFile = <path> macros/fonts/LiberationMono-V2.ttf
  MakeFace = true
  Placement = pos=(464.8,96.9594,0) rot=(0,0,1;0rad)
  Size = 25.5
  Tracking = 0
FEATURE [Part::Part2DObjectPython] ShapeString156  # Draft 2D object (typed FeaturePython)
  FontFile = <path> macros/fonts/LiberationMono-V2.ttf
  MakeFace = true
  Placement = pos=(64.8,63.6261,0) rot=(0,0,1;0rad)
  Size = 25.5
  Tracking = 0
FEATURE [Part::Part2DObjectPython] ShapeString157  # Draft 2D object (typed FeaturePython)
  FontFile = <path> macros/fonts/LiberationMono-V2.ttf
  MakeFace = true
  Placement = pos=(98.1333,63.6261,0) rot=(0,0,1;0rad)
  Size = 25.5
  Tracking = 0
FEATURE [Part::Part2DObjectPython] ShapeString158  # Draft 2D object (typed FeaturePython)
  FontFile = <path> macros/fonts/LiberationMono-V2.ttf
  MakeFace = true
  Placement = pos=(131.467,63.6261,0) rot=(0,0,1;0rad)
  Size = 25.5
  Tracking = 0
FEATURE [Part::Part2DObjectPython] ShapeString159  # Draft 2D object (typed FeaturePython)
  FontFile = <path> macros/fonts/LiberationMono-V2.ttf
  MakeFace = true
  Placement = pos=(164.8,63.6261,0) rot=(0,0,1;0rad)
  Size = 25.5
  Tracking = 0
FEATURE [Part::Part2DObjectPython] ShapeString160  # Draft 2D object (typed FeaturePython)
  FontFile = <path> macros/fonts/LiberationMono-V2.ttf
  MakeFace = true
  Placement = pos=(198.133,63.6261,0) rot=(0,0,1;0rad)
  Size = 25.5
  Tracking = 0
FEATURE [Part::Part2DObjectPython] ShapeString161  # Draft 2D object (typed FeaturePython)
  FontFile = <path> macros/fonts/LiberationMono-V2.ttf
  MakeFace = true
  Placement = pos=(231.467,63.6261,0) rot=(0,0,1;0rad)
  Size = 25.5
  Tracking = 0
FEATURE [Part::Part2DObjectPython] ShapeString162  # Draft 2D object (typed FeaturePython)
  FontFile = <path> macros/fonts/LiberationMono-V2.ttf
  MakeFace = true
  Placement = pos=(264.8,63.6261,0) rot=(0,0,1;0rad)
  Size = 25.5
  Tracking = 0
FEATURE [Part::Part2DObjectPython] ShapeString163  # Draft 2D object (typed FeaturePython)
  FontFile = <path> macros/fonts/LiberationMono-V2.ttf
  MakeFace = true
  Placement = pos=(298.133,63.6261,0) rot=(0,0,1;0rad)
  Size = 25.5
  Tracking = 0
FEATURE [Part::Part2DObjectPython] ShapeString164  # Draft 2D object (typed FeaturePython)
  FontFile = <path> macros/fonts/LiberationMono-V2.ttf
  MakeFace = true
  Placement = pos=(331.467,63.6261,0) rot=(0,0,1;0rad)
  Size = 25.5
  Tracking = 0
FEATURE [Part::Part2DObjectPython] ShapeString165  # Draft 2D object (typed FeaturePython)
  FontFile = <path> macros/fonts/LiberationMono-V2.ttf
  MakeFace = true
  Placement = pos=(364.8,63.6261,0) rot=(0,0,1;0rad)
  Size = 25.5
  Tracking = 0
FEATURE [Part::Part2DObjectPython] ShapeString166  # Draft 2D object (typed FeaturePython)
  FontFile = <path> macros/fonts/LiberationMono-V2.ttf
  MakeFace = true
  Placement = pos=(398.133,63.6261,0) rot=(0,0,1;0rad)
  Size = 25.5
  Tracking = 0
FEATURE [Part::Part2DObjectPython] ShapeString167  # Draft 2D object (typed FeaturePython)
  FontFile = <path> macros/fonts/LiberationMono-V2.ttf
  MakeFace = true
  Placement = pos=(431.467,63.6261,0) rot=(0,0,1;0rad)
  Size = 25.5
  Tracking = 0
FEATURE [Part::Part2DObjectPython] ShapeString168  # Draft 2D object (typed FeaturePython)
  FontFile = <path> macros/fonts/LiberationMono-V2.ttf
  MakeFace = true
  Placement = pos=(464.8,63.6261,0) rot=(0,0,1;0rad)
  Size = 25.5
  Tracking = 0
FEATURE [Part::Part2DObjectPython] Rectangle  # Draft 2D object (typed FeaturePython)
  Area = 0
  ChamferSize = 0
  Columns = 1
  FilletRadius = 0
  Height = 550
  Length = 550
  MakeFace = true
  Rows = 1
FEATURE [App::Part] Part
  Group = -> [Circle,ShapeString,ShapeString001,ShapeString002,ShapeString003,ShapeString004,ShapeString005,ShapeString006,ShapeString007,ShapeString008,ShapeString009,ShapeString010,ShapeString011,ShapeString012,ShapeString013,ShapeString014,ShapeString015,ShapeString016,ShapeString017,ShapeString018,ShapeString019,ShapeString020,ShapeString021,ShapeString022,ShapeString023,ShapeString024,ShapeString025,+144 more]
  Origin = -> Origin
note: 166 file-system paths scrubbed to <path> (originals preserved in the JSON sidecar)
